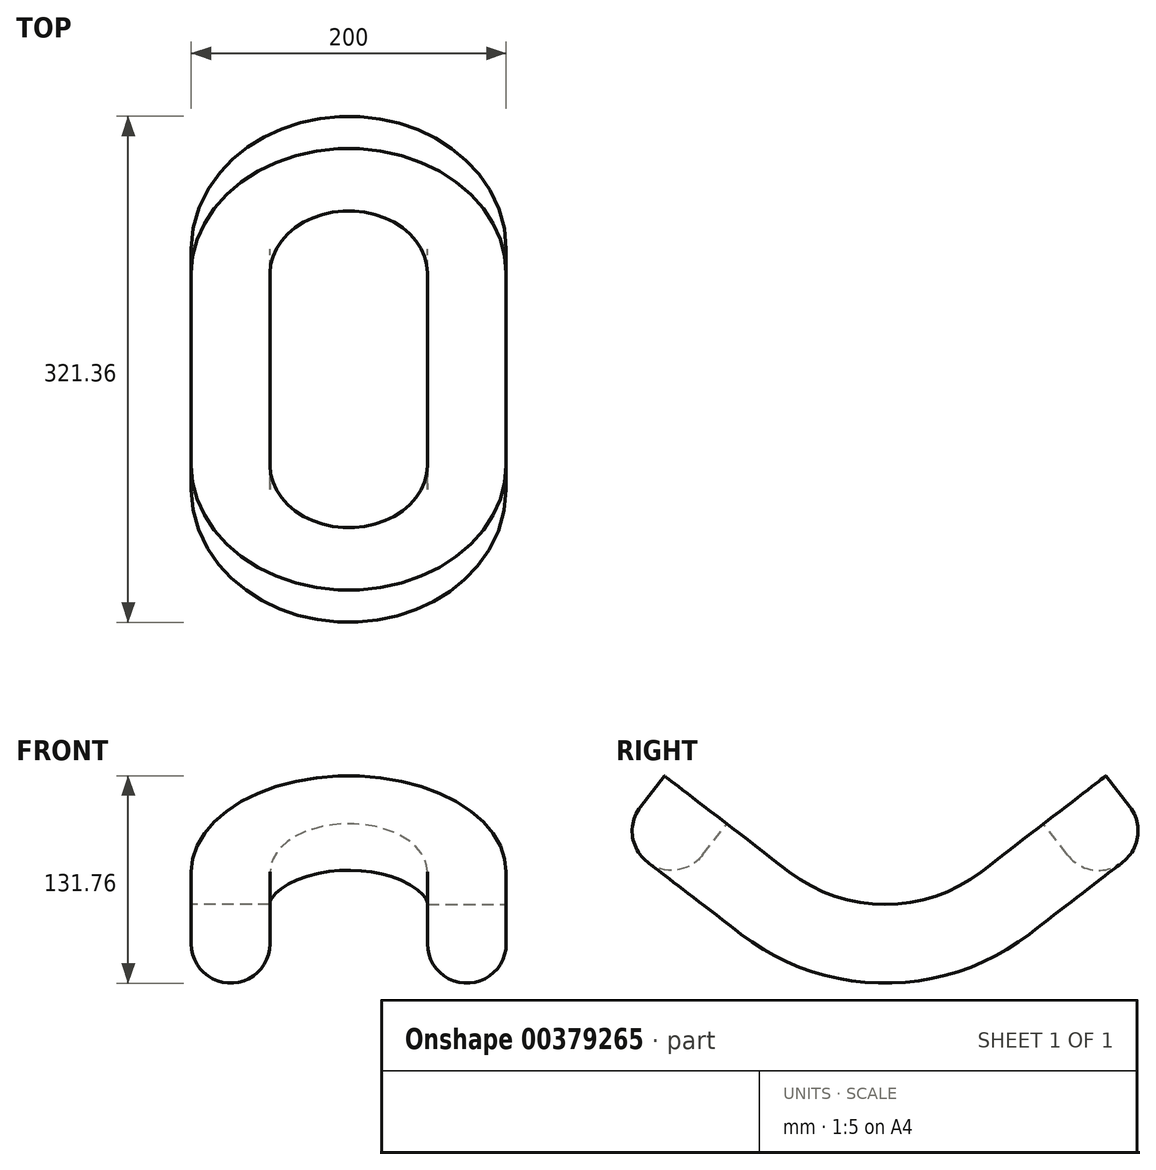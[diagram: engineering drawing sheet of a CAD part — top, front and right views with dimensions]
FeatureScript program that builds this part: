
annotation { "Feature Type Name" : "Feature", "Feature Type Description" : "" }
export const myFeature = defineFeature(function(context is Context, id is Id, definition is map)
    precondition{}
    {
        {
            var Q0;
            Q0=qCreatedBy(makeId("Right.planeOp"),FACE);
            var sketch = newSketch(context, id + "F0", { "sketchPlane" : qUnion([Q0])});
            skArc(sketch, "E0", {"start": v(0, 0) * mm, "mid": v(48.32, 8) * mm, "end": v(91.5, 31.14) * mm});
            skLineSegment(sketch, "E1", {"start": v(91.5, 31.14) * mm, "end": v(170.74, 92.14) * mm});
            skSolve(sketch);
        }
        {
            var Q0;
            Q0=sQuery(id+"F0.wireOp",EDGE,"E0");
            var Q1;
            Q1=sQuery(id+"F0.wireOp",EDGE,"E1");
            extrude(context, id + "F1", {"bodyType" : ToolBodyType.SURFACE, "surfaceEntities" : qUnion([Q0, Q1]), "depth" : 100 * mm});
        }
        {
            var Q0;
            Q0=makeQuery(id+"F1.opExtrude","SWEPT_FACE",FACE,{"disambiguationData":[OSD([sQuery(id+"F0.wireOp",EDGE,"E1")])]});
            var sketch = newSketch(context, id + "F2", { "sketchPlane" : qUnion([Q0])});
            skArc(sketch, "E2", {"start": v(0, -191.5) * mm, "mid": v(70.71, -162.2) * mm, "end": v(100, -91.5) * mm});
            skSolve(sketch);
        }
        {
            var Q0;
            Q0=qCreatedBy(makeId("Front.planeOp"),FACE);
            var sketch = newSketch(context, id + "F3", { "sketchPlane" : qUnion([Q0])});
            skLineSegment(sketch, "E3.bottom", {"start": v(50, 50) * mm, "end": v(100, 50) * mm});
            skLineSegment(sketch, "E3.top", {"start": v(50, 0) * mm, "end": v(100, 0) * mm});
            skLineSegment(sketch, "E3.left", {"start": v(50, 50) * mm, "end": v(50, 0) * mm});
            skLineSegment(sketch, "E3.right", {"start": v(100, 50) * mm, "end": v(100, 0) * mm});
            skLineSegment(sketch, "E4", {"start": v(50, 25) * mm, "end": v(100, 25) * mm, "construction": true});
            skPoint(sketch, "E4.endSnap0", {"position": v(100, 25) * mm});
            skLineSegment(sketch, "E5", {"start": v(75, 50) * mm, "end": v(75, 0) * mm, "construction": true});
            skArc(sketch, "E6", {"start": v(100, 25) * mm, "mid": v(75, 0) * mm, "end": v(50, 25) * mm});
            skSolve(sketch);
        }
        {
            var Q0;
            {var subQ5=sQuery(id+"F3.wireOp",EDGE,"E3.bottom");Q0=makeQuery(id+"F3.imprint","IMPRINT",FACE,{"disambiguationData":[TD([[makeQuery(id+"F3.imprint","IMPRINT",EDGE,{"derivedFrom":subQ5}),-1.0]])]});}
            var Q1;
            Q1=makeQuery(id+"F1.opExtrude","CAP_EDGE",EDGE,{"disambiguationData":[OSD([sQuery(id+"F0.wireOp",EDGE,"E0")])],"isStart":false});
            var Q2;
            Q2=sQuery(id+"F2.wireOp",EDGE,"E2");
            sweep(context, id + "F4", {"profiles" : qUnion([Q0]), "path" : qUnion([Q1, Q2])});
        }
        {
            var Q0;
            Q0=makeQuery(id+"F4.opSweep","SWEPT_BODY",BODY,{"disambiguationData":[OSD([sQuery(id+"F2.wireOp",EDGE,"E2"),sQuery(id+"F3.wireOp",EDGE,"E3.bottom"),sQuery(id+"F3.wireOp",EDGE,"E3.left"),sQuery(id+"F3.wireOp",EDGE,"E3.right"),sQuery(id+"F3.wireOp",EDGE,"E6")])]});
            var Q1;
            Q1=qCreatedBy(makeId("Right.planeOp"),FACE);
            mirror(context, id + "F5", {"operationType" : NewBodyOperationType.ADD, "entities" : qUnion([Q0]), "mirrorPlane" : qUnion([Q1])});
        }
        {
            var Q0;
            Q0=makeQuery(id+"F4.opSweep","SWEPT_BODY",BODY,{"disambiguationData":[OSD([sQuery(id+"F2.wireOp",EDGE,"E2"),sQuery(id+"F3.wireOp",EDGE,"E3.bottom"),sQuery(id+"F3.wireOp",EDGE,"E3.left"),sQuery(id+"F3.wireOp",EDGE,"E3.right"),sQuery(id+"F3.wireOp",EDGE,"E6")])]});
            var Q1;
            Q1=qCreatedBy(makeId("Front.planeOp"),FACE);
            mirror(context, id + "F6", {"operationType" : NewBodyOperationType.ADD, "entities" : qUnion([Q0]), "mirrorPlane" : qUnion([Q1])});
        }
    });
